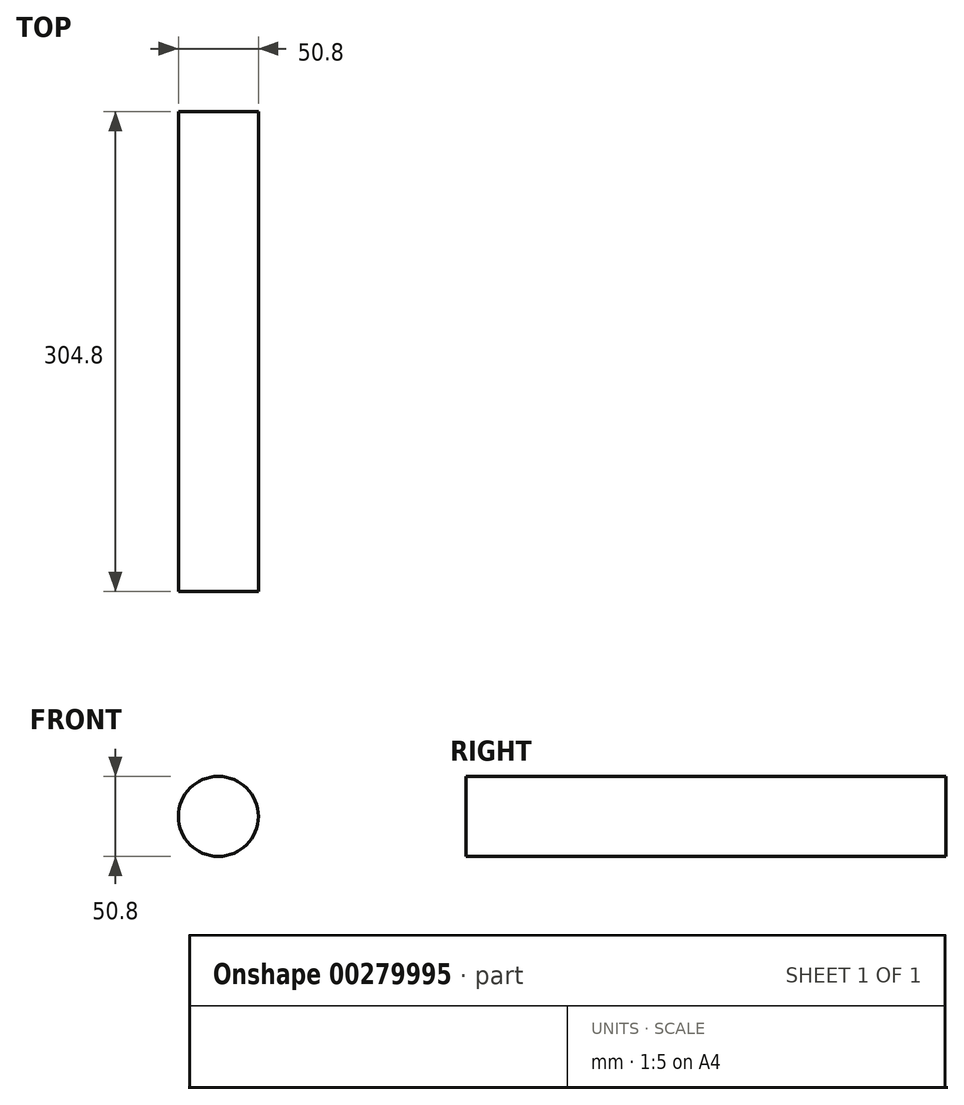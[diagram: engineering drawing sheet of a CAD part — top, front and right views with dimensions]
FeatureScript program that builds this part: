
annotation { "Feature Type Name" : "Feature", "Feature Type Description" : "" }
export const myFeature = defineFeature(function(context is Context, id is Id, definition is map)
    precondition{}
    {
        {
            var Q0;
            Q0=qCreatedBy(makeId("Front.planeOp"),FACE);
            var sketch = newSketch(context, id + "F0", { "sketchPlane" : qUnion([Q0])});
            skCircle(sketch, "E0", {"center": v(0, 0) * mm, "radius": 25.4 * mm});
            skSolve(sketch);
        }
        {
            var Q0;
            Q0=makeQuery(id+"F0.imprint","IMPRINT",FACE,{"disambiguationData":[TD([[makeQuery(id+"F0.imprint","IMPRINT",EDGE,{"derivedFrom":sQuery(id+"F0.wireOp",EDGE,"E0")}),1.0]])]});
            extrude(context, id + "F1", {"entities" : qUnion([Q0]), "depth" : 304.8 * mm});
        }
    });
